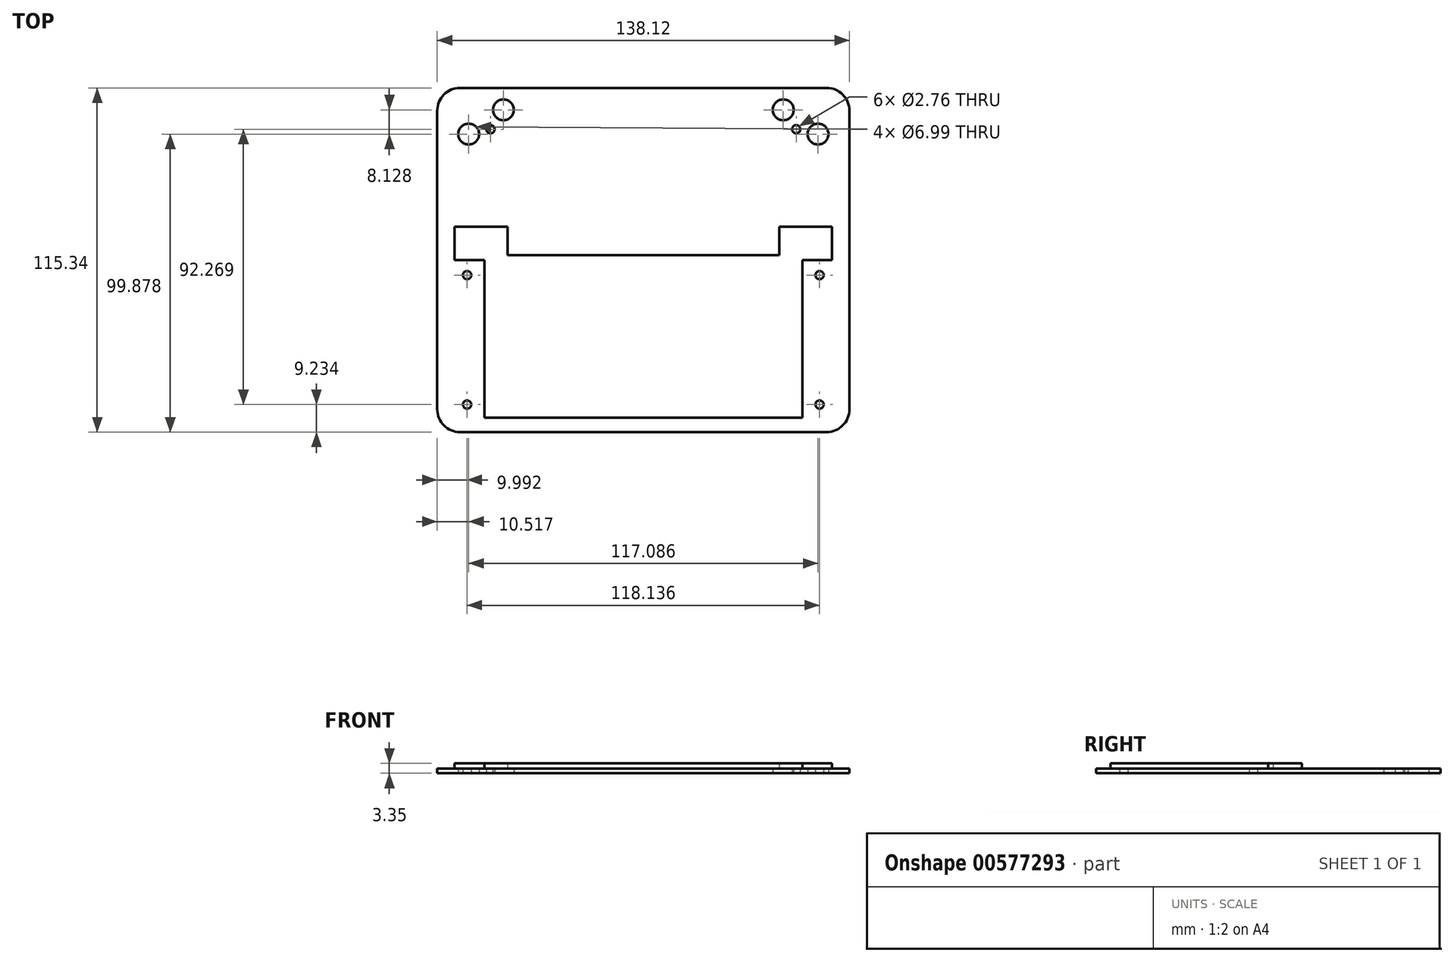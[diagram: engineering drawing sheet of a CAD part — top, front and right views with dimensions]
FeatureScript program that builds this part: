
annotation { "Feature Type Name" : "Feature", "Feature Type Description" : "" }
export const myFeature = defineFeature(function(context is Context, id is Id, definition is map)
    precondition{}
    {
        {
            var Q0;
            Q0=qCreatedBy(makeId("Top.planeOp"),FACE);
            var sketch = newSketch(context, id + "F0", { "sketchPlane" : qUnion([Q0])});
            skLineSegment(sketch, "E0.bottom", {"start": v(69.06, 57.67) * mm, "end": v(-69.06, 57.67) * mm});
            skLineSegment(sketch, "E0.top", {"start": v(69.06, -57.67) * mm, "end": v(-69.06, -57.67) * mm});
            skLineSegment(sketch, "E0.left", {"start": v(69.06, 57.67) * mm, "end": v(69.06, -57.67) * mm});
            skLineSegment(sketch, "E0.right", {"start": v(-69.06, 57.67) * mm, "end": v(-69.06, -57.67) * mm});
            skPoint(sketch, "E0.middle", {"position": v(0, 0) * mm});
            skCircle(sketch, "E1", {"center": v(-46.9, 50.34) * mm, "radius": 3.5 * mm});
            skCircle(sketch, "E2", {"center": v(-58.54, 42.2) * mm, "radius": 3.5 * mm});
            skCircle(sketch, "E3", {"center": v(-51.23, 43.83) * mm, "radius": 1.38 * mm});
            skCircle(sketch, "E4", {"center": v(-59.07, -5.05) * mm, "radius": 1.38 * mm});
            skCircle(sketch, "E5", {"center": v(-59.07, -48.44) * mm, "radius": 1.38 * mm});
            skLineSegment(sketch, "E6", {"start": v(-59.07, -48.44) * mm, "end": v(-59.07, -5.05) * mm, "construction": true});
            skLineSegment(sketch, "E7", {"start": v(0, 57.67) * mm, "end": v(0, -57.67) * mm, "construction": true});
            skCircle(sketch, "E8.MirrorC", {"center": v(59.07, -48.44) * mm, "radius": 1.38 * mm});
            skCircle(sketch, "E9.MirrorC", {"center": v(59.07, -5.05) * mm, "radius": 1.38 * mm});
            skCircle(sketch, "E10.MirrorC", {"center": v(58.54, 42.2) * mm, "radius": 3.5 * mm});
            skCircle(sketch, "E11.MirrorC", {"center": v(51.23, 43.83) * mm, "radius": 1.38 * mm});
            skCircle(sketch, "E12.MirrorC", {"center": v(46.9, 50.34) * mm, "radius": 3.5 * mm});
            skSolve(sketch);
        }
        {
            var Q0;
            Q0 = qSketchRegion(id + "F0", true);
            extrude(context, id + "F1", {"entities" : qUnion([Q0]), "depth" : 1.52 * mm, "offsetDistance" : 25.4 * mm});
        }
        {
            var Q0;
            Q0=makeQuery(id+"F1.opExtrude","CAP_FACE",FACE,{"disambiguationData":[OSD([sQuery(id+"F0.wireOp",EDGE,"E0.bottom"),sQuery(id+"F0.wireOp",EDGE,"E0.top"),sQuery(id+"F0.wireOp",EDGE,"E0.left"),sQuery(id+"F0.wireOp",EDGE,"E0.right"),sQuery(id+"F0.wireOp",EDGE,"E1"),sQuery(id+"F0.wireOp",EDGE,"E2"),sQuery(id+"F0.wireOp",EDGE,"E3"),sQuery(id+"F0.wireOp",EDGE,"E4"),sQuery(id+"F0.wireOp",EDGE,"E5"),sQuery(id+"F0.wireOp",EDGE,"E8.MirrorC"),sQuery(id+"F0.wireOp",EDGE,"E9.MirrorC"),sQuery(id+"F0.wireOp",EDGE,"E10.MirrorC"),sQuery(id+"F0.wireOp",EDGE,"E11.MirrorC"),sQuery(id+"F0.wireOp",EDGE,"E12.MirrorC")])],"isStart":false});
            var sketch = newSketch(context, id + "F2", { "sketchPlane" : qUnion([Q0])});
            skLineSegment(sketch, "E13", {"start": v(0, 57.67) * mm, "end": v(0, -57.67) * mm, "construction": true});
            skLineSegment(sketch, "E14", {"start": v(0, -52.9) * mm, "end": v(-53.29, -52.9) * mm});
            skLineSegment(sketch, "E15", {"start": v(-53.29, -52.9) * mm, "end": v(-53.29, 0) * mm});
            skLineSegment(sketch, "E16", {"start": v(-53.29, 0) * mm, "end": v(-63.22, 0) * mm});
            skLineSegment(sketch, "E17", {"start": v(-63.22, 0) * mm, "end": v(-63.22, 11.21) * mm});
            skLineSegment(sketch, "E18", {"start": v(-63.22, 11.21) * mm, "end": v(-45.52, 11.21) * mm});
            skLineSegment(sketch, "E19", {"start": v(-45.52, 11.21) * mm, "end": v(-45.52, 1.64) * mm});
            skLineSegment(sketch, "E20", {"start": v(-45.52, 1.64) * mm, "end": v(0, 1.64) * mm});
            skLineSegment(sketch, "E21.MirrorCS", {"start": v(45.52, 11.21) * mm, "end": v(45.52, 1.64) * mm});
            skLineSegment(sketch, "E22.MirrorCS", {"start": v(45.52, 1.64) * mm, "end": v(0, 1.64) * mm});
            skLineSegment(sketch, "E23.MirrorCS", {"start": v(63.22, 11.21) * mm, "end": v(45.52, 11.21) * mm});
            skLineSegment(sketch, "E24.MirrorCS", {"start": v(63.22, 0) * mm, "end": v(63.22, 11.21) * mm});
            skLineSegment(sketch, "E25.MirrorCS", {"start": v(53.29, 0) * mm, "end": v(63.22, 0) * mm});
            skLineSegment(sketch, "E26.MirrorCS", {"start": v(53.29, -52.9) * mm, "end": v(53.29, 0) * mm});
            skLineSegment(sketch, "E27.MirrorCS", {"start": v(0, -52.9) * mm, "end": v(53.29, -52.9) * mm});
            skSolve(sketch);
        }
        {
            var Q0;
            Q0 = qSketchRegion(id + "F2", true);
            extrude(context, id + "F3", {"entities" : qUnion([Q0]), "operationType" : NewBodyOperationType.ADD, "depth" : 1.83 * mm, "offsetDistance" : 25.4 * mm});
        }
        {
            var Q0;
            Q0=makeQuery(id+"F1.opExtrude","SWEPT_EDGE",EDGE,{"disambiguationData":[OSD([sQuery(id+"F0.wireOp",EDGE,"E0.bottom"),sQuery(id+"F0.wireOp",EDGE,"E0.right")])]});
            var Q1;
            Q1=makeQuery(id+"F1.opExtrude","SWEPT_EDGE",EDGE,{"disambiguationData":[OSD([sQuery(id+"F0.wireOp",EDGE,"E0.bottom"),sQuery(id+"F0.wireOp",EDGE,"E0.left")])]});
            var Q2;
            Q2=makeQuery(id+"F1.opExtrude","SWEPT_EDGE",EDGE,{"disambiguationData":[OSD([sQuery(id+"F0.wireOp",EDGE,"E0.top"),sQuery(id+"F0.wireOp",EDGE,"E0.left")])]});
            var Q3;
            Q3=makeQuery(id+"F1.opExtrude","SWEPT_EDGE",EDGE,{"disambiguationData":[OSD([sQuery(id+"F0.wireOp",EDGE,"E0.top"),sQuery(id+"F0.wireOp",EDGE,"E0.right")])]});
            fillet(context, id + "F4", {"entities" : qUnion([Q0, Q1, Q2, Q3]), "radius" : 7.62 * mm, "tangentPropagation" : true, "allowEdgeOverflow" : false});
        }
    });
